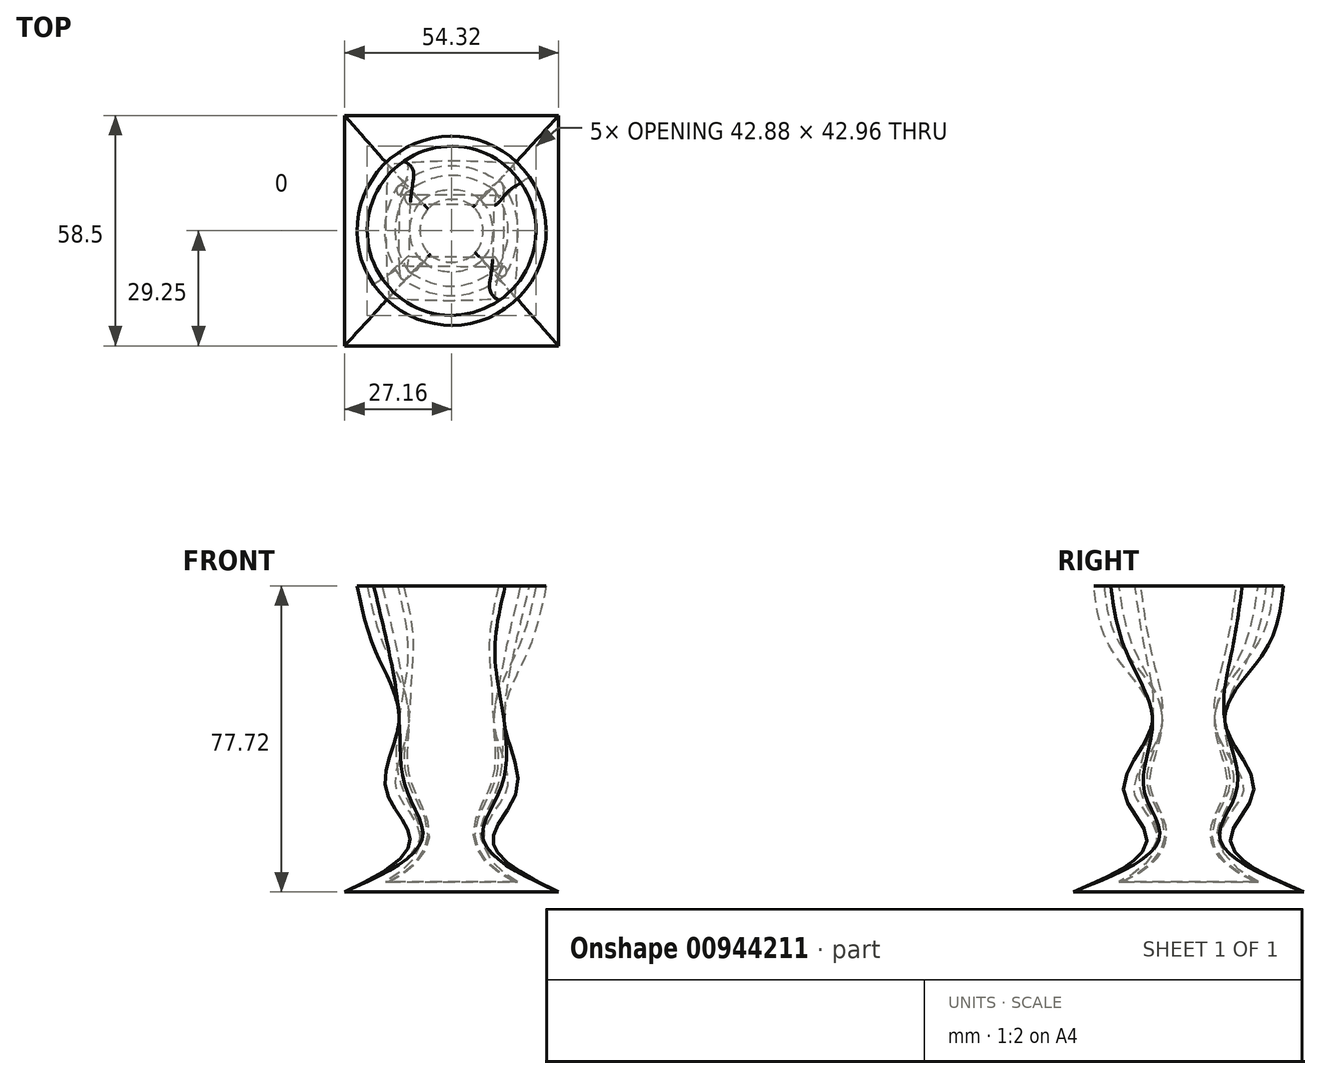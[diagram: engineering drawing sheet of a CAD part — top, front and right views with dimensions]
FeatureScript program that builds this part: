
annotation { "Feature Type Name" : "Feature", "Feature Type Description" : "" }
export const myFeature = defineFeature(function(context is Context, id is Id, definition is map)
    precondition{}
    {
        {
            var Q0;
            Q0=qCreatedBy(makeId("Top.planeOp"),FACE);
            var sketch = newSketch(context, id + "F0", { "sketchPlane" : qUnion([Q0])});
            skLineSegment(sketch, "E0.bottom", {"start": v(27.16, 29.25) * mm, "end": v(-27.16, 29.25) * mm});
            skLineSegment(sketch, "E0.top", {"start": v(27.16, -29.25) * mm, "end": v(-27.16, -29.25) * mm});
            skLineSegment(sketch, "E0.left", {"start": v(27.16, 29.25) * mm, "end": v(27.16, -29.25) * mm});
            skLineSegment(sketch, "E0.right", {"start": v(-27.16, 29.25) * mm, "end": v(-27.16, -29.25) * mm});
            skPoint(sketch, "E0.middle", {"position": v(0, 0) * mm});
            skSolve(sketch);
        }
        {
            var Q0;
            Q0=qCreatedBy(makeId("Top.planeOp"),FACE);
            cPlane(context, id + "F1", {"entities" : qUnion([Q0]), "cplaneType" : CPlaneType.OFFSET, "offset" : 77.72 * mm, "width" : 152.4 * mm, "height" : 152.4 * mm});
        }
        {
            var Q0;
            Q0=qCreatedBy(id+"F1.planeOp",FACE);
            var sketch = newSketch(context, id + "F2", { "sketchPlane" : qUnion([Q0])});
            skCircle(sketch, "E1", {"center": v(0, 0) * mm, "radius": 24.04 * mm});
            skSolve(sketch);
        }
        {
            var Q0;
            Q0=qCreatedBy(makeId("Top.planeOp"),FACE);
            cPlane(context, id + "F3", {"entities" : qUnion([Q0]), "cplaneType" : CPlaneType.OFFSET, "offset" : 14.73 * mm, "width" : 152.4 * mm, "height" : 152.4 * mm});
        }
        {
            var Q0;
            Q0=qCreatedBy(makeId("Top.planeOp"),FACE);
            cPlane(context, id + "F4", {"entities" : qUnion([Q0]), "cplaneType" : CPlaneType.OFFSET, "offset" : 25.4 * mm, "width" : 152.4 * mm, "height" : 152.4 * mm});
        }
        {
            var Q0;
            Q0=qCreatedBy(makeId("Top.planeOp"),FACE);
            cPlane(context, id + "F5", {"entities" : qUnion([Q0]), "cplaneType" : CPlaneType.OFFSET, "offset" : 61.2 * mm, "width" : 152.4 * mm, "height" : 152.4 * mm});
        }
        {
            var Q0;
            Q0=qCreatedBy(makeId("Top.planeOp"),FACE);
            cPlane(context, id + "F6", {"entities" : qUnion([Q0]), "cplaneType" : CPlaneType.OFFSET, "offset" : 43.69 * mm, "width" : 152.4 * mm, "height" : 152.4 * mm});
        }
        {
            var Q0;
            Q0=qCreatedBy(id+"F3.planeOp",FACE);
            var sketch = newSketch(context, id + "F7", { "sketchPlane" : qUnion([Q0])});
            skCircle(sketch, "E2", {"center": v(0, 0) * mm, "radius": 10.73 * mm});
            skSolve(sketch);
        }
        {
            var Q0;
            Q0=qCreatedBy(id+"F4.planeOp",FACE);
            var sketch = newSketch(context, id + "F8", { "sketchPlane" : qUnion([Q0])});
            skCircle(sketch, "E3", {"center": v(0, 0) * mm, "radius": 16.54 * mm});
            skSolve(sketch);
        }
        {
            var Q0;
            Q0=qCreatedBy(id+"F6.planeOp",FACE);
            var sketch = newSketch(context, id + "F9", { "sketchPlane" : qUnion([Q0])});
            skLineSegment(sketch, "E4.bottom", {"start": v(13.3, 9.16) * mm, "end": v(-13.3, 9.16) * mm});
            skLineSegment(sketch, "E4.top", {"start": v(13.3, -9.16) * mm, "end": v(-13.3, -9.16) * mm});
            skLineSegment(sketch, "E4.left", {"start": v(13.3, 9.16) * mm, "end": v(13.3, -9.16) * mm});
            skLineSegment(sketch, "E4.right", {"start": v(-13.3, 9.16) * mm, "end": v(-13.3, -9.16) * mm});
            skPoint(sketch, "E4.middle", {"position": v(0, 0) * mm});
            skSolve(sketch);
        }
        {
            var Q0;
            Q0=qCreatedBy(id+"F5.planeOp",FACE);
            var sketch = newSketch(context, id + "F10", { "sketchPlane" : qUnion([Q0])});
            skCircle(sketch, "E5", {"center": v(0, 0) * mm, "radius": 19.38 * mm});
            skSolve(sketch);
        }
        {
            var Q0;
            Q0=makeQuery(id+"F0.imprint","IMPRINT",FACE,{"disambiguationData":[TD([[makeQuery(id+"F0.imprint","IMPRINT",EDGE,{"derivedFrom":sQuery(id+"F0.wireOp",EDGE,"E0.bottom")}),1.0]])]});
            var Q1;
            Q1=makeQuery(id+"F7.imprint","IMPRINT",FACE,{"disambiguationData":[TD([[makeQuery(id+"F7.imprint","IMPRINT",EDGE,{"derivedFrom":sQuery(id+"F7.wireOp",EDGE,"E2")}),1.0]])]});
            var Q2;
            Q2=makeQuery(id+"F8.imprint","IMPRINT",FACE,{"disambiguationData":[TD([[makeQuery(id+"F8.imprint","IMPRINT",EDGE,{"derivedFrom":sQuery(id+"F8.wireOp",EDGE,"E3")}),1.0]])]});
            var Q3;
            Q3=makeQuery(id+"F9.imprint","IMPRINT",FACE,{"disambiguationData":[TD([[makeQuery(id+"F9.imprint","IMPRINT",EDGE,{"derivedFrom":sQuery(id+"F9.wireOp",EDGE,"E4.bottom")}),1.0]])]});
            var Q4;
            Q4=makeQuery(id+"F10.imprint","IMPRINT",FACE,{"disambiguationData":[TD([[makeQuery(id+"F10.imprint","IMPRINT",EDGE,{"derivedFrom":sQuery(id+"F10.wireOp",EDGE,"E5")}),1.0]])]});
            var Q5;
            Q5=makeQuery(id+"F2.imprint","IMPRINT",FACE,{"disambiguationData":[TD([[makeQuery(id+"F2.imprint","IMPRINT",EDGE,{"derivedFrom":sQuery(id+"F2.wireOp",EDGE,"E1")}),1.0]])]});
            loft(context, id + "F11", {"sheetProfilesArray" : [{ "sheetProfileEntities" : qUnion([Q0]) }, { "sheetProfileEntities" : qUnion([Q1]) }, { "sheetProfileEntities" : qUnion([Q2]) }, { "sheetProfileEntities" : qUnion([Q3]) }, { "sheetProfileEntities" : qUnion([Q4]) }, { "sheetProfileEntities" : qUnion([Q5]) }]});
        }
        {
            var Q0;
            Q0=makeQuery(id+"F11.opLoft","CAP_FACE",FACE,{"disambiguationData":[OSD([makeQuery(id+"F2.imprint","IMPRINT",FACE,{"disambiguationData":[TD([[makeQuery(id+"F2.imprint","IMPRINT",EDGE,{"derivedFrom":sQuery(id+"F2.wireOp",EDGE,"E1")}),1.0]])]})])],"isStart":true});
            shell(context, id + "F12", {"entities" : qUnion([Q0]), "thickness" : 2.54 * mm});
        }
    });
